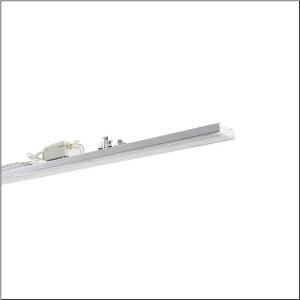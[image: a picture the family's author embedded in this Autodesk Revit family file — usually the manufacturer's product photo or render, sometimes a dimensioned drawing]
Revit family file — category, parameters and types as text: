
# Revit family: licross_21_recessed_mo_52te12dn495g
name_source: partatom
category: Lighting Fixtures
units: mm (PartAtom-declared; Revit-internal decimal feet)

## family parameters
Cut with Voids When Loaded = No
Host = Face
Light Source = No
Part Type = Normal
Room Calculation Point = No
Round Connector Dimension = Use Diameter
Shared = No

## types (1)
- --- (1 x LED, 9520 lm, 53.3 W, 4000K)
    Apparent Load = 53 VA
    CIE Flux Codes = 72 92 99 100 100
    Color Rendering = 80
    Color Temperature = 4000K
    Default Elevation = 1800 mm
    Description = Licross 21 Recessed MO, luminaire insert, of sheet steel, galvanised, coil coated, white, length: 1.500mm, width: 66mm, height: 67mm, LED rated luminous flux: 9.520lm, light colour: 840, SDCM (Standard Deviation of Colour Matching)MacAdam ≤ 3 SDCM (initial), control gear: DALI 2, with plug, 5-pole, with phase selection, mains connection: 220..240V, AC, 50/60Hz, rated input power: 53W, internal wiring halogen-free, primary optical cover: cover, of PMMA, light emission: direct distribution, primary light characteristic: symmetric, protection rating (complete): IP54, insulation class (complete): insulation class I (protective earthing), certification: CE, ENEC, VDE, UKCA, protection symbol: D if used in an environment with non-conductive dust loads with corresponding accessories, impact resistance: IK06, permissible ambient temperature for indoor applications: -25..+35°C, corresponds to IFS (International Featured Standards) requirements for safety and quality in the food industry, reducing of maximum allowable ambient temperature of 5°C with ceiling mounting, LABS conformity tested according to VDMA 24364:2018-05, The light source and the operating device comply with the requirements of the Ecodesign Regulation (EU) 2019/2020 and are replaceable in accordance with this regulation, packaging unit: 1 piece
    Height = 58 mm
    Lamp = 1 x LED
    Lamp Light Flux = 9520 lm
    Lamp Power = 53.3 W
    Lamp count = 1
    Length = 1500 mm
    Luminous efficacy = 179 lm/W
    Manufacturer = Siteco
    ModVariant = No
    Model = 52TE12DN495G
    Mounting Place = Ceiling
    Mounting Type = Pendant
    Number of Poles = 1
    OnlyDefault = Yes
    Power Factor = 1
    Product Name = Licross 21 Recessed MO
    Product group = luminaire insert | ceiling pendant
    ProductGroupID = 901
    Protection Class = Protection class I
    Protection Degree = IP 54
    RLX_Detail_Level = 1
    RLX_Emergency_Light_Flux = 0 lm
    RLX_Emergency_Type = 0
    RLX_Emergency_Type_DB = No
    RlxData = <blob elided: 24973 chars, md5=52279cd4>
    Socket = socket
    Standby Power = 0 W
    System Light Flux = 9520 lm
    System Power = 53 W
    Type Comments = factory setting: luminous flux: 100 % | dim-lin: 254 | 359 mA
    Type Image = l_1296930.jpg
    URL = http://relux.com
    VarID = @adj_088225
    Voltage = 0 V
    Weight = 0.00 kg
    Width = 66 mm

## geometry (parser evidence)
native form markers: Blend x4, Sweep x9
no freeform markers — native parametric forms only
